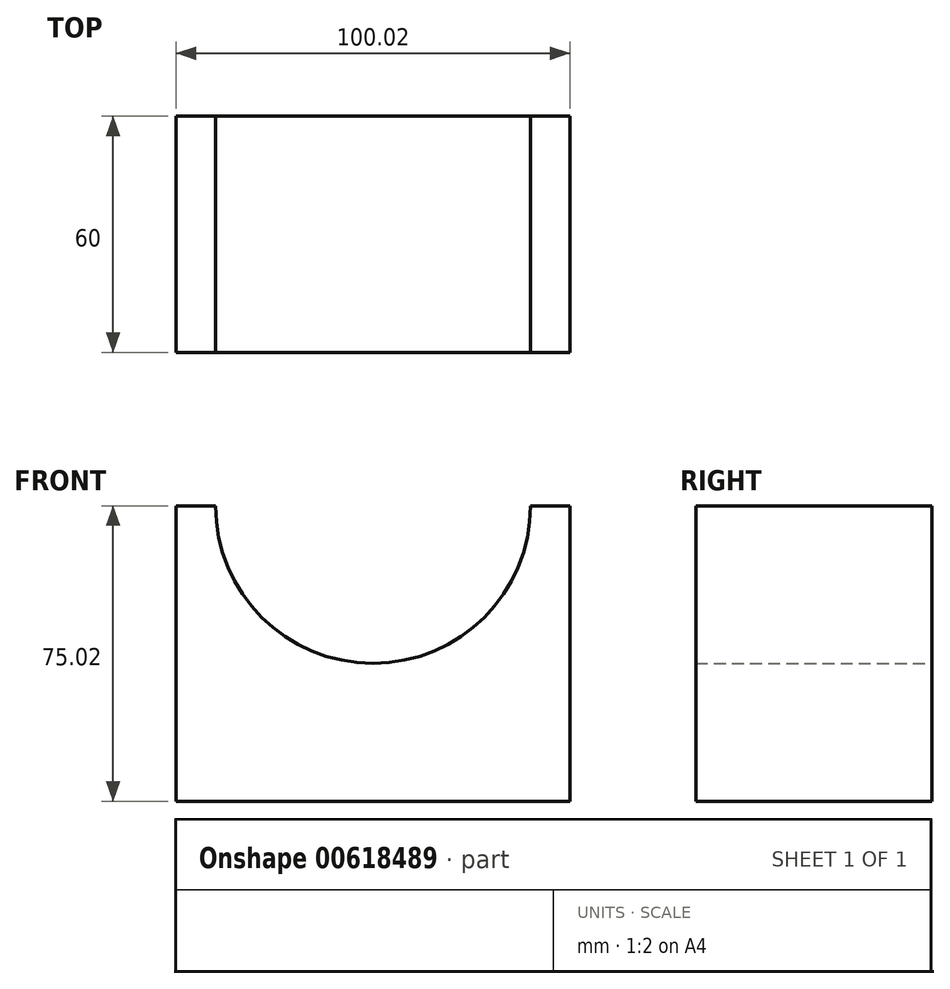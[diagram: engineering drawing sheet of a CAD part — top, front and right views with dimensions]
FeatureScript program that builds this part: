
annotation { "Feature Type Name" : "Feature", "Feature Type Description" : "" }
export const myFeature = defineFeature(function(context is Context, id is Id, definition is map)
    precondition{}
    {
        {
            var Q0;
            Q0=qCreatedBy(makeId("Front.planeOp"),FACE);
            var sketch = newSketch(context, id + "F0", { "sketchPlane" : qUnion([Q0])});
            skLineSegment(sketch, "E0.bottom", {"start": v(50, -37.5) * mm, "end": v(-50, -37.5) * mm});
            skLineSegment(sketch, "E0.top", {"start": v(50, 37.5) * mm, "end": v(-50, 37.5) * mm});
            skLineSegment(sketch, "E0.left", {"start": v(50, -37.5) * mm, "end": v(50, 37.5) * mm});
            skLineSegment(sketch, "E0.right", {"start": v(-50, -37.5) * mm, "end": v(-50, 37.5) * mm});
            skPoint(sketch, "E0.middle", {"position": v(0, 0) * mm});
            skCircle(sketch, "E1", {"center": v(0, 37.5) * mm, "radius": 40 * mm});
            skSolve(sketch);
        }
        {
            var Q0;
            Q0=makeQuery(id+"F0.imprint","IMPRINT",FACE,{"disambiguationData":[TD([[makeQuery(id+"F0.imprint","IMPRINT",EDGE,{"derivedFrom":sQuery(id+"F0.wireOp",EDGE,"E0.bottom")}),-1.0]])]});
            extrude(context, id + "F1", {"entities" : qUnion([Q0]), "depth" : 60 * mm, "offsetDistance" : 25 * mm});
        }
    });
